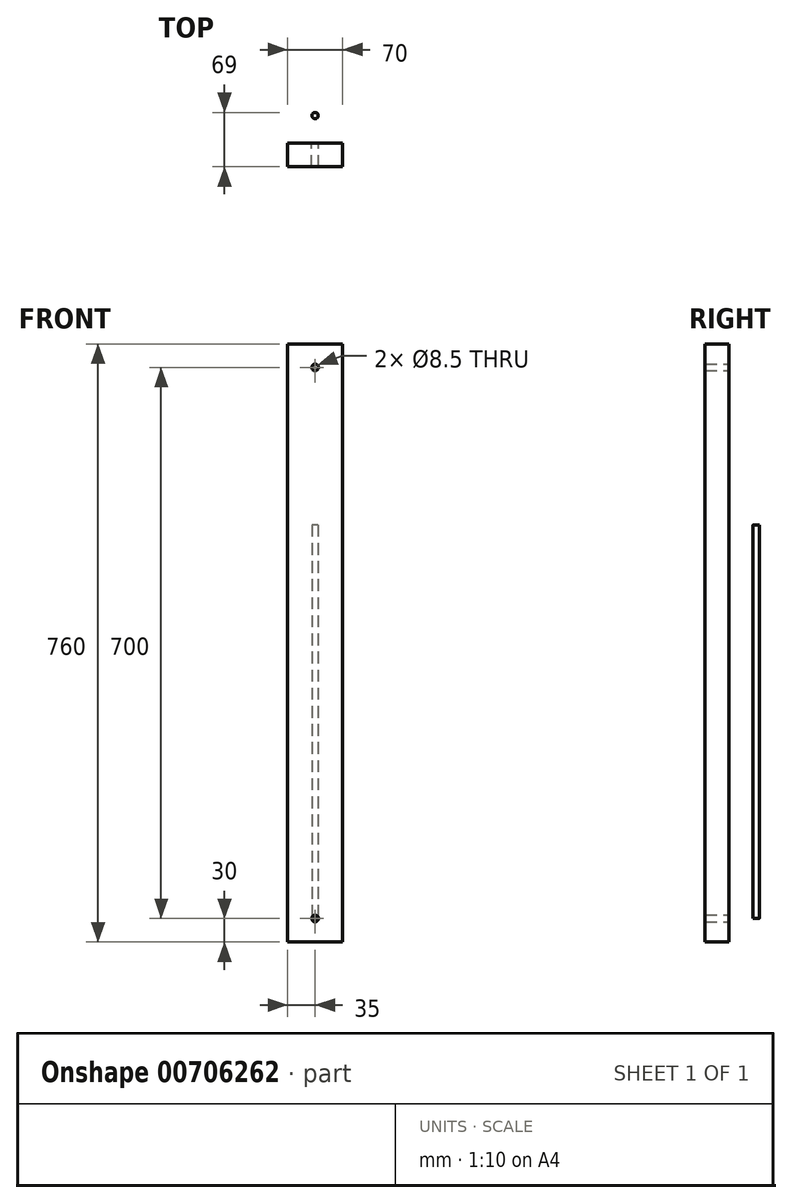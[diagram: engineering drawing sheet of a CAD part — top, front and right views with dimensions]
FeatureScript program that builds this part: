
annotation { "Feature Type Name" : "Feature", "Feature Type Description" : "" }
export const myFeature = defineFeature(function(context is Context, id is Id, definition is map)
    precondition{}
    {
        {
            var Q0;
            Q0=qCreatedBy(makeId("Front.planeOp"),FACE);
            var sketch = newSketch(context, id + "F0", { "sketchPlane" : qUnion([Q0])});
            skLineSegment(sketch, "E0", {"start": v(0, 0) * mm, "end": v(0, 700) * mm});
            skLineSegment(sketch, "E1", {"start": v(0, 700) * mm, "end": v(0, 730) * mm});
            skLineSegment(sketch, "E2", {"start": v(0, 730) * mm, "end": v(35, 730) * mm});
            skLineSegment(sketch, "E3", {"start": v(35, 730) * mm, "end": v(35, 0) * mm});
            skLineSegment(sketch, "E4", {"start": v(35, 0) * mm, "end": v(35, -30) * mm});
            skLineSegment(sketch, "E5", {"start": v(35, -30) * mm, "end": v(0, -30) * mm});
            skLineSegment(sketch, "E6", {"start": v(0, -30) * mm, "end": v(-35, -30) * mm});
            skLineSegment(sketch, "E7", {"start": v(-35, -30) * mm, "end": v(-35, 0) * mm});
            skLineSegment(sketch, "E8", {"start": v(-35, 0) * mm, "end": v(-35, 730) * mm});
            skLineSegment(sketch, "E9", {"start": v(-35, 730) * mm, "end": v(0, 730) * mm});
            skCircle(sketch, "E10", {"center": v(0, 700) * mm, "radius": 4.25 * mm});
            skCircle(sketch, "E11", {"center": v(0, 0) * mm, "radius": 4.25 * mm});
            skSolve(sketch);
        }
        {
            var Q0;
            Q0 = qSketchRegion(id + "F0", true);
            extrude(context, id + "F1", {"entities" : qUnion([Q0]), "endBound" : BoundingType.SYMMETRIC, "depth" : 30 * mm, "offsetDistance" : 25 * mm});
        }
        {
            var Q0;
            Q0=qCreatedBy(makeId("Top.planeOp"),FACE);
            var sketch = newSketch(context, id + "F2", { "sketchPlane" : qUnion([Q0])});
            skLineSegment(sketch, "E12", {"start": v(0, 0) * mm, "end": v(0, 50) * mm});
            skCircle(sketch, "E13", {"center": v(0, 50) * mm, "radius": 4 * mm});
            skSolve(sketch);
        }
        {
            var Q0;
            Q0 = qSketchRegion(id + "F2", true);
            extrude(context, id + "F3", {"entities" : qUnion([Q0]), "depth" : 500 * mm, "offsetDistance" : 25 * mm});
        }
    });
